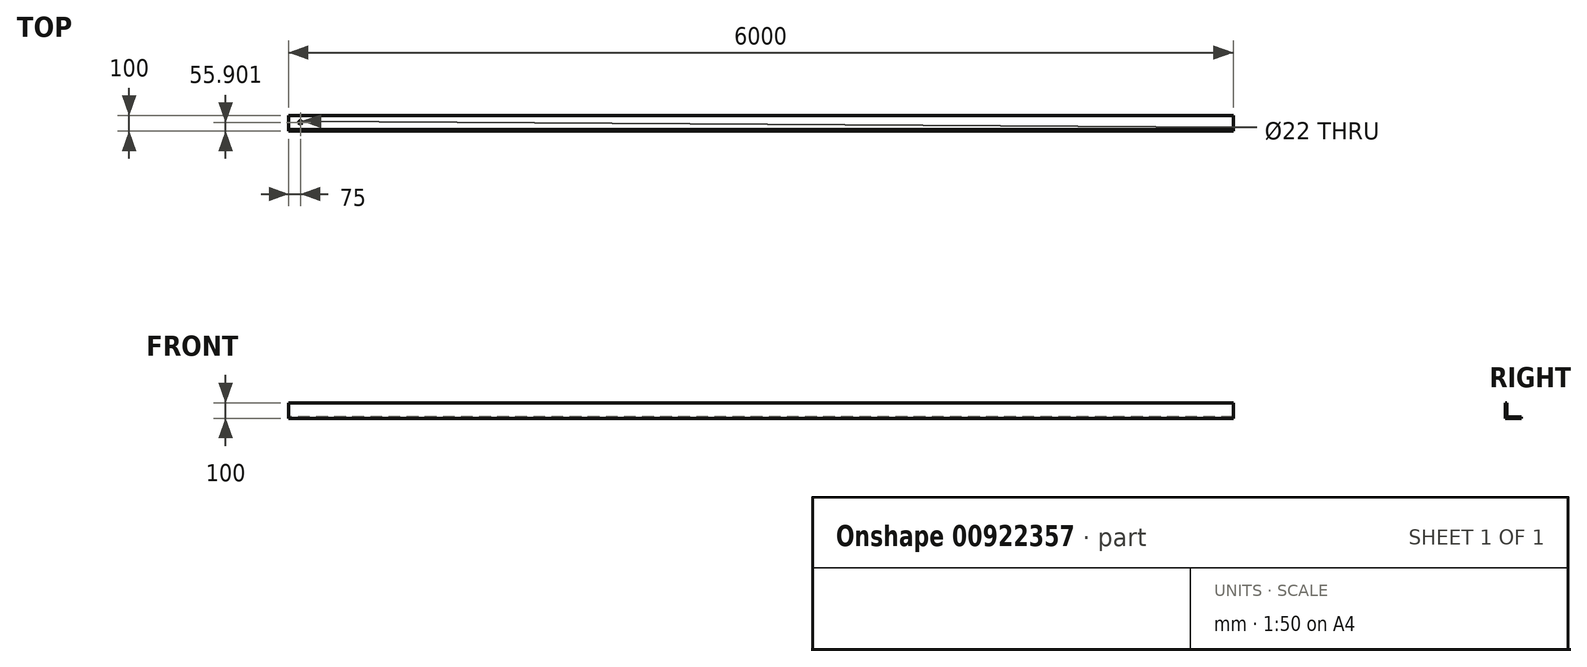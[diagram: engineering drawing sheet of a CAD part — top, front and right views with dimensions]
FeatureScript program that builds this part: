
annotation { "Feature Type Name" : "Feature", "Feature Type Description" : "" }
export const myFeature = defineFeature(function(context is Context, id is Id, definition is map)
    precondition{}
    {
        {
            var Q0;
            Q0=qCreatedBy(makeId("Right.planeOp"),FACE);
            var sketch = newSketch(context, id + "F0", { "sketchPlane" : qUnion([Q0])});
            skLineSegment(sketch, "E0", {"start": v(0, 0) * mm, "end": v(0, 100) * mm});
            skLineSegment(sketch, "E1", {"start": v(0, 100) * mm, "end": v(10, 100) * mm});
            skLineSegment(sketch, "E2", {"start": v(10, 100) * mm, "end": v(10, 10) * mm});
            skLineSegment(sketch, "E3", {"start": v(10, 10) * mm, "end": v(100, 10) * mm});
            skLineSegment(sketch, "E4", {"start": v(100, 10) * mm, "end": v(100, 0) * mm});
            skLineSegment(sketch, "E5", {"start": v(100, 0) * mm, "end": v(0, 0) * mm});
            skSolve(sketch);
        }
        {
            var Q0;
            Q0 = qSketchRegion(id + "F0", true);
            extrude(context, id + "F1", {"entities" : qUnion([Q0]), "depth" : 6000 * mm, "offsetDistance" : 25 * mm});
        }
        {
            var Q0;
            Q0=qCreatedBy(makeId("Top.planeOp"),FACE);
            var sketch = newSketch(context, id + "F2", { "sketchPlane" : qUnion([Q0])});
            skLineSegment(sketch, "E6", {"start": v(0, 0) * mm, "end": v(75, 0) * mm});
            skLineSegment(sketch, "E7", {"start": v(75, 108.9) * mm, "end": v(75, 0) * mm});
            skLineSegment(sketch, "E8", {"start": v(0, 100.9) * mm, "end": v(0, 55.9) * mm});
            skLineSegment(sketch, "E9", {"start": v(75, 55.9) * mm, "end": v(0, 55.9) * mm});
            skCircle(sketch, "E10", {"center": v(75, 55.9) * mm, "radius": 13 * mm});
            skSolve(sketch);
        }
        {
            var Q0;
            Q0=sQuery(id+"F2.wireOp",VERTEX,"E10.center");
            var Q1;
            Q1=makeQuery(id+"F1.opExtrude","SWEPT_BODY",BODY,{"disambiguationData":[OSD([sQuery(id+"F0.wireOp",EDGE,"E0"),sQuery(id+"F0.wireOp",EDGE,"E1"),sQuery(id+"F0.wireOp",EDGE,"E2"),sQuery(id+"F0.wireOp",EDGE,"E3"),sQuery(id+"F0.wireOp",EDGE,"E4"),sQuery(id+"F0.wireOp",EDGE,"E5")])]});
            hole(context, id + "F3", {"style" : HoleStyle.SIMPLE, "endStyle" : HoleEndStyle.THROUGH, "oppositeDirection" : true, "standardTappedOrClearance" : lookupTablePath({ "fit" : "Normal", "standard" : "ISO", "size" : "M20", "type" : "Clearance" }), "standardBlindInLast" : lookupTablePath({ "fit" : "Normal", "standard" : "ISO", "size" : "M20", "type" : "Clearance" }), "holeDiameter" : 22 * mm, "majorDiameter" : 5 * mm, "isTappedThrough" : true, "tappedDepth" : 14.75 * mm, "tapClearance" : 3, "locations" : qUnion([Q0]), "scope" : qUnion([Q1])});
        }
    });
